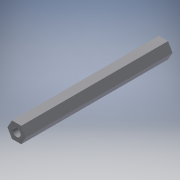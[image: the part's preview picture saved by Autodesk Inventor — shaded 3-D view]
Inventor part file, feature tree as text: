
AUTODESK INVENTOR PART (.ipt)
format: ipt  version: 2017 (Build 210142000, 142)  size: 152,576 bytes
history: native  units: in
note: dims shown in document units (in); Inventor stores cm internally (conversion verified against a paired STEP export)
features: other x4, hole x1, extrude x1, sketch x1, reference x1
ambient origin geometry x8: Origin, YZ Plane, XZ Plane, XY Plane, X Axis, Y Axis, Z Axis, Center Point
bodies: Solid1 (feature_tree)
feature tree (8):
  hole  "Hole1"  [1 undecoded]
  extrude  "Extrusion1"  Depth=1.0in
  sketch  "Sketch1"  dims[d0=0.25in d1=0.25in d2=0.2656in d3=0.75in d4=0.375in d5=0.25in d6=0.5635in d7=20.0in d8=0.8108in d9=1.0in d10=0.0in d11=0.25in d12=0.0in]
  reference  "Reference1"
  other  "Default:1"
  parser-record x1  (decoder bookkeeping rows leaked as tree rows — omitted from the tree; the rows remain in map.json)
  other  "SideFrame.iam"
  other  "#35_12T_Sprocket:2"
note: 1 required parameter value undecoded (feature->parameter linkage not recoverable at this tier; creation-order binding heuristic only, values carry confidence <= 0.55)
note: 1 file-system path scrubbed to <path> (originals preserved in map.json)
